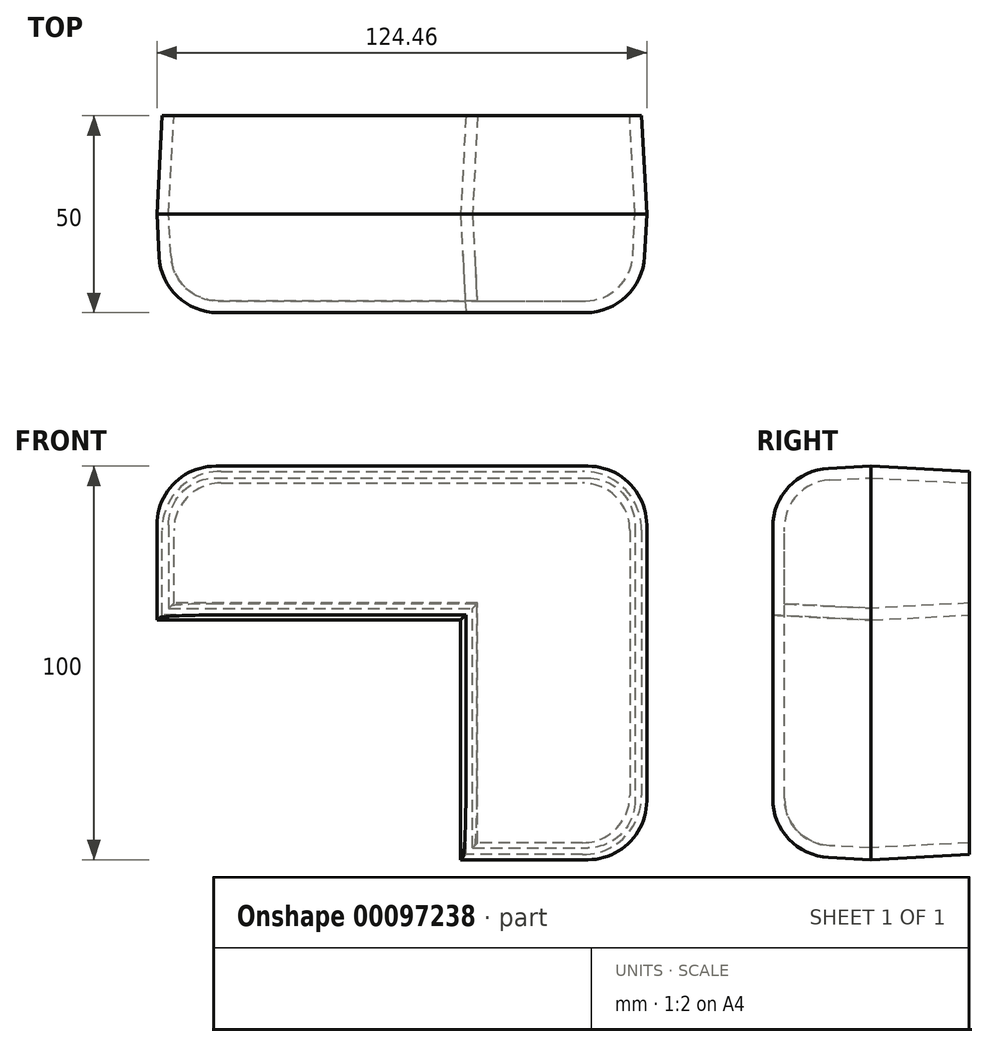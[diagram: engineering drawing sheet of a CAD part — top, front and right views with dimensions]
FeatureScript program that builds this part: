
annotation { "Feature Type Name" : "Feature", "Feature Type Description" : "" }
export const myFeature = defineFeature(function(context is Context, id is Id, definition is map)
    precondition{}
    {
        {
            var Q0;
            Q0=qCreatedBy(makeId("Front.planeOp"),FACE);
            var sketch = newSketch(context, id + "F0", { "sketchPlane" : qUnion([Q0])});
            skLineSegment(sketch, "E0.bottom", {"start": v(0, 100) * mm, "end": v(124.46, 100) * mm});
            skLineSegment(sketch, "E0.top", {"start": v(0, 0) * mm, "end": v(124.46, 0) * mm});
            skLineSegment(sketch, "E0.left", {"start": v(0, 100) * mm, "end": v(0, 0) * mm});
            skLineSegment(sketch, "E0.right", {"start": v(124.46, 100) * mm, "end": v(124.46, 0) * mm});
            skLineSegment(sketch, "E1.bottom", {"start": v(0, 0) * mm, "end": v(77.17, 0) * mm});
            skLineSegment(sketch, "E1.top", {"start": v(0, 60.87) * mm, "end": v(77.17, 60.87) * mm});
            skLineSegment(sketch, "E1.left", {"start": v(0, 0) * mm, "end": v(0, 60.87) * mm});
            skLineSegment(sketch, "E1.right", {"start": v(77.17, 0) * mm, "end": v(77.17, 60.87) * mm});
            skLineSegment(sketch, "E2.bottom", {"start": v(77.17, 60.87) * mm, "end": v(43.48, 60.87) * mm});
            skLineSegment(sketch, "E2.top", {"start": v(77.17, 29.9) * mm, "end": v(43.48, 29.9) * mm});
            skLineSegment(sketch, "E2.left", {"start": v(77.17, 60.87) * mm, "end": v(77.17, 29.9) * mm});
            skLineSegment(sketch, "E2.right", {"start": v(43.48, 60.87) * mm, "end": v(43.48, 29.9) * mm});
            skSolve(sketch);
        }
        {
            var Q0;
            Q0=makeQuery(id+"F0.imprint","IMPRINT",FACE,{"disambiguationData":[TD([[makeQuery(id+"F0.imprint","IMPRINT",EDGE,{"derivedFrom":sQuery(id+"F0.wireOp",EDGE,"E0.bottom")}),-1.0]])]});
            var Q1;
            Q1=makeQuery(id+"F0.imprint","IMPRINT",FACE,{"disambiguationData":[TD([[makeQuery(id+"F0.imprint","IMPRINT",EDGE,{"derivedFrom":sQuery(id+"F0.wireOp",EDGE,"E1.bottom")}),1.0]])]});
            extrude(context, id + "F1", {"entities" : qUnion([Q0, Q1]), "endBound" : BoundingType.SYMMETRIC, "depth" : 50 * mm, "hasDraft" : true, "draftAngle" : 3 * degree, "draftPullDirection" : true});
        }
        {
            var Q0;
            Q0=makeQuery(id+"F1.opExtrude","CAP_EDGE",EDGE,{"disambiguationData":[OSD([sQuery(id+"F0.wireOp",EDGE,"E0.bottom")])],"isStart":false});
            var Q1;
            Q1=makeQuery(id+"F1.split0.splitOp","SPLIT",EDGE,{"derivedFrom":makeQuery(id+"F1.opExtrude","SWEPT_EDGE",EDGE,{"disambiguationData":[OSD([sQuery(id+"F0.wireOp",EDGE,"E0.bottom"),sQuery(id+"F0.wireOp",EDGE,"E0.right")])]})});
            var Q2;
            Q2=makeQuery(id+"F1.split0.splitOp","SPLIT",EDGE,{"derivedFrom":makeQuery(id+"F1.opExtrude","SWEPT_EDGE",EDGE,{"disambiguationData":[OSD([sQuery(id+"F0.wireOp",EDGE,"E0.bottom"),sQuery(id+"F0.wireOp",EDGE,"E0.right")])]}),"isFromBackBody":true});
            var Q3;
            Q3=makeQuery(id+"F1.opExtrude","CAP_EDGE",EDGE,{"disambiguationData":[OSD([sQuery(id+"F0.wireOp",EDGE,"E0.right")])],"isStart":false});
            var Q4;
            Q4=makeQuery(id+"F1.opExtrude","CAP_EDGE",EDGE,{"disambiguationData":[OSD([sQuery(id+"F0.wireOp",EDGE,"E0.left"),sQuery(id+"F0.wireOp",EDGE,"E1.left")])],"isStart":false});
            var Q5;
            Q5=makeQuery(id+"F1.opExtrude","CAP_EDGE",EDGE,{"disambiguationData":[OSD([sQuery(id+"F0.wireOp",EDGE,"E0.top"),sQuery(id+"F0.wireOp",EDGE,"E1.bottom")])],"isStart":false});
            var Q6;
            Q6=makeQuery(id+"F1.opExtrude","CAP_EDGE",EDGE,{"disambiguationData":[OSD([sQuery(id+"F0.wireOp",EDGE,"E2.bottom")])],"isStart":false});
            var Q7;
            Q7=makeQuery(id+"F1.opExtrude","CAP_EDGE",EDGE,{"disambiguationData":[OSD([sQuery(id+"F0.wireOp",EDGE,"E2.right")])],"isStart":false});
            var Q8;
            Q8=makeQuery(id+"F1.opExtrude","CAP_EDGE",EDGE,{"disambiguationData":[OSD([sQuery(id+"F0.wireOp",EDGE,"E2.top")])],"isStart":false});
            var Q9;
            Q9=makeQuery(id+"F1.opExtrude","CAP_EDGE",EDGE,{"disambiguationData":[OSD([sQuery(id+"F0.wireOp",EDGE,"E2.left")])],"isStart":false});
            var Q10;
            Q10=makeQuery(id+"F1.split0.splitOp","SPLIT",EDGE,{"derivedFrom":makeQuery(id+"F1.opExtrude","SWEPT_EDGE",EDGE,{"disambiguationData":[OSD([sQuery(id+"F0.wireOp",EDGE,"E0.top"),sQuery(id+"F0.wireOp",EDGE,"E0.right")])]})});
            var Q11;
            Q11=makeQuery(id+"F1.split0.splitOp","SPLIT",EDGE,{"derivedFrom":makeQuery(id+"F1.opExtrude","SWEPT_EDGE",EDGE,{"disambiguationData":[OSD([sQuery(id+"F0.wireOp",EDGE,"E0.top"),sQuery(id+"F0.wireOp",EDGE,"E0.right")])]}),"isFromBackBody":true});
            var Q12;
            Q12=makeQuery(id+"F1.split0.splitOp","SPLIT",EDGE,{"derivedFrom":makeQuery(id+"F1.opExtrude","SWEPT_EDGE",EDGE,{"disambiguationData":[OSD([sQuery(id+"F0.wireOp",EDGE,"E1.bottom"),sQuery(id+"F0.wireOp",EDGE,"E1.left")])]}),"isFromBackBody":true});
            var Q13;
            Q13=makeQuery(id+"F1.split0.splitOp","SPLIT",EDGE,{"derivedFrom":makeQuery(id+"F1.opExtrude","SWEPT_EDGE",EDGE,{"disambiguationData":[OSD([sQuery(id+"F0.wireOp",EDGE,"E1.bottom"),sQuery(id+"F0.wireOp",EDGE,"E1.left")])]})});
            var Q14;
            Q14=makeQuery(id+"F1.split0.splitOp","SPLIT",EDGE,{"derivedFrom":makeQuery(id+"F1.opExtrude","SWEPT_EDGE",EDGE,{"disambiguationData":[OSD([sQuery(id+"F0.wireOp",EDGE,"E0.bottom"),sQuery(id+"F0.wireOp",EDGE,"E0.left")])]}),"isFromBackBody":true});
            var Q15;
            Q15=makeQuery(id+"F1.split0.splitOp","SPLIT",EDGE,{"derivedFrom":makeQuery(id+"F1.opExtrude","SWEPT_EDGE",EDGE,{"disambiguationData":[OSD([sQuery(id+"F0.wireOp",EDGE,"E0.bottom"),sQuery(id+"F0.wireOp",EDGE,"E0.left")])]})});
            fillet(context, id + "F2", {"entities" : qUnion([Q0, Q1, Q2, Q3, Q4, Q5, Q6, Q7, Q8, Q9, Q10, Q11, Q12, Q13, Q14, Q15]), "radius" : 15 * mm, "tangentPropagation" : true, "allowEdgeOverflow" : false});
        }
        {
            var Q0;
            Q0=makeQuery(id+"F1.opExtrude","CAP_FACE",FACE,{"disambiguationData":[OSD([sQuery(id+"F0.wireOp",EDGE,"E0.bottom"),sQuery(id+"F0.wireOp",EDGE,"E0.top"),sQuery(id+"F0.wireOp",EDGE,"E0.left"),sQuery(id+"F0.wireOp",EDGE,"E0.right"),sQuery(id+"F0.wireOp",EDGE,"E1.bottom"),sQuery(id+"F0.wireOp",EDGE,"E1.left"),sQuery(id+"F0.wireOp",EDGE,"E2.bottom"),sQuery(id+"F0.wireOp",EDGE,"E2.top"),sQuery(id+"F0.wireOp",EDGE,"E2.left"),sQuery(id+"F0.wireOp",EDGE,"E2.right")])],"isStart":true});
            shell(context, id + "F3", {"entities" : qUnion([Q0]), "thickness" : 3 * mm});
        }
    });
